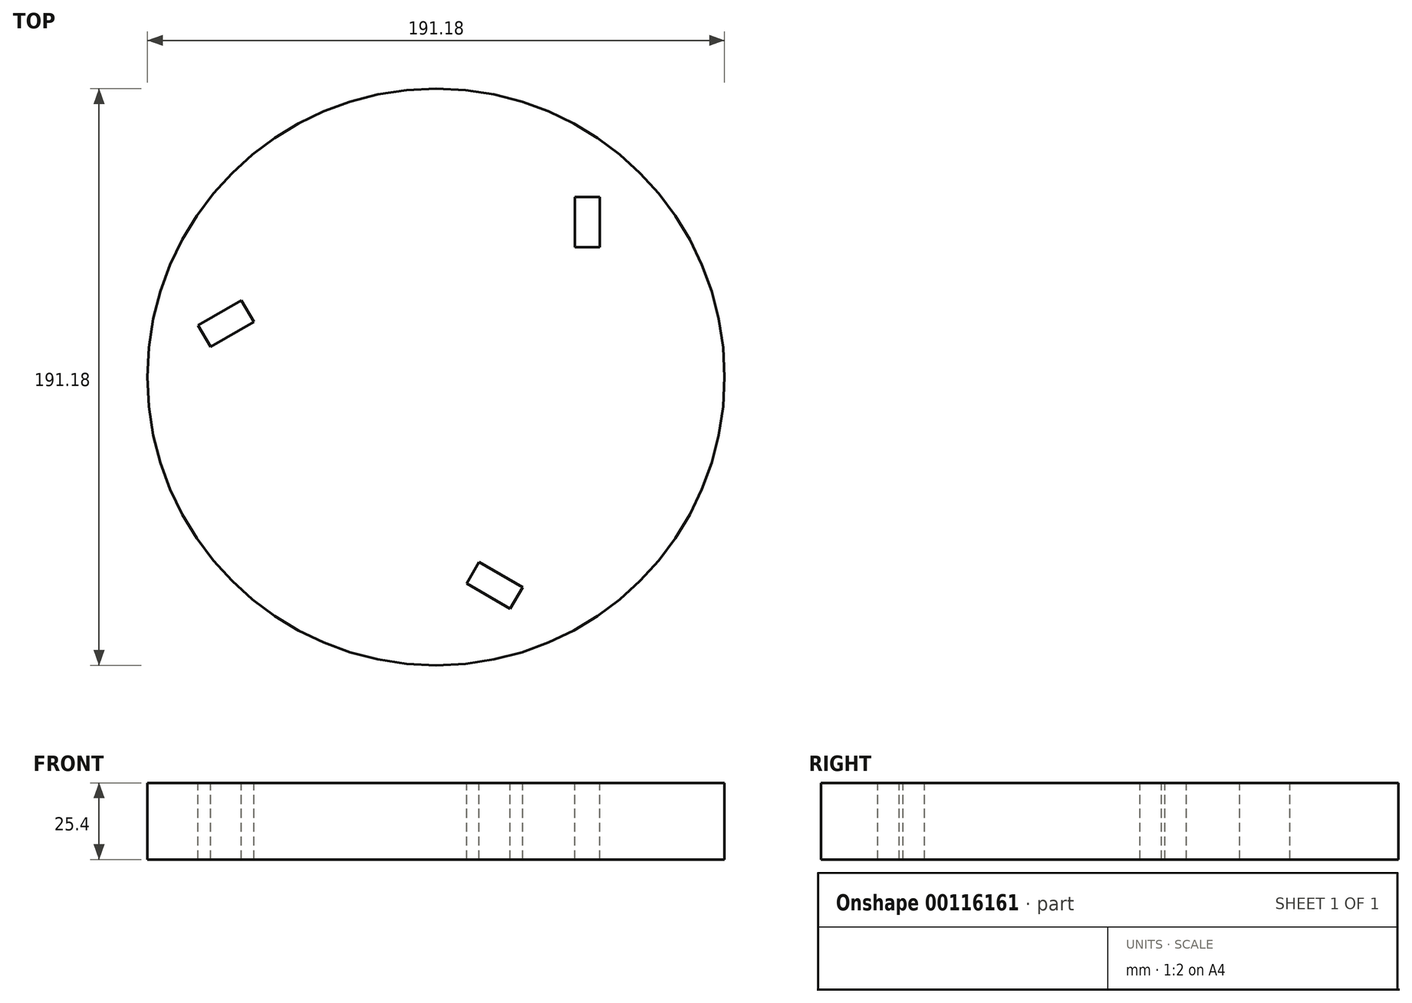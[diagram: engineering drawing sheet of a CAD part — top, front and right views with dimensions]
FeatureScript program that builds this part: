
annotation { "Feature Type Name" : "Feature", "Feature Type Description" : "" }
export const myFeature = defineFeature(function(context is Context, id is Id, definition is map)
    precondition{}
    {
        {
            var Q0;
            Q0=qCreatedBy(makeId("Top.planeOp"),FACE);
            var sketch = newSketch(context, id + "F0", { "sketchPlane" : qUnion([Q0])});
            skLineSegment(sketch, "E0.bottom", {"start": v(54.23, 59.68) * mm, "end": v(46.03, 59.68) * mm});
            skLineSegment(sketch, "E0.top", {"start": v(54.23, 43.09) * mm, "end": v(46.03, 43.09) * mm});
            skLineSegment(sketch, "E0.left", {"start": v(54.23, 59.68) * mm, "end": v(54.23, 43.09) * mm});
            skLineSegment(sketch, "E0.right", {"start": v(46.03, 59.68) * mm, "end": v(46.03, 43.09) * mm});
            skLineSegment(sketch, "E1.1.0", {"start": v(-64.43, 25.43) * mm, "end": v(-60.33, 18.32) * mm});
            skLineSegment(sketch, "E1.1.1", {"start": v(-78.8, 17.13) * mm, "end": v(-64.43, 25.43) * mm});
            skLineSegment(sketch, "E1.1.2", {"start": v(-78.8, 17.13) * mm, "end": v(-74.7, 10.03) * mm});
            skLineSegment(sketch, "E1.1.3", {"start": v(-74.7, 10.03) * mm, "end": v(-60.33, 18.32) * mm});
            skLineSegment(sketch, "E1.2.0", {"start": v(10.2, -68.51) * mm, "end": v(14.3, -61.4) * mm});
            skLineSegment(sketch, "E1.2.1", {"start": v(24.56, -76.8) * mm, "end": v(10.2, -68.51) * mm});
            skLineSegment(sketch, "E1.2.2", {"start": v(24.56, -76.8) * mm, "end": v(28.66, -69.7) * mm});
            skLineSegment(sketch, "E1.2.3", {"start": v(28.66, -69.7) * mm, "end": v(14.3, -61.4) * mm});
            skPoint(sketch, "E1.center", {"position": v(0, 0) * mm});
            skSolve(sketch);
        }
        {
            var Q0;
            Q0=sQuery(id+"F0.wireOp",EDGE,"E1.2.1");
            var Q1;
            Q1 = qBodyType(qCreatedBy(id + "F0" ,EDGE), BodyType.WIRE);
            extrude(context, id + "F3", {"bodyType" : ToolBodyType.SURFACE, "surfaceEntities" : qUnion([Q0, Q1]), "depth" : 25.4 * mm});
        }
        {
            var Q0;
            Q0=qCreatedBy(makeId("Top.planeOp"),FACE);
            var sketch = newSketch(context, id + "F1", { "sketchPlane" : qUnion([Q0])});
            skCircle(sketch, "E2", {"center": v(0, 0) * mm, "radius": 95.59 * mm});
            skSolve(sketch);
        }
        {
            var Q0;
            Q0=makeQuery(id+"F1.imprint","IMPRINT",FACE,{"disambiguationData":[TD([[makeQuery(id+"F1.imprint","IMPRINT",EDGE,{"derivedFrom":sQuery(id+"F1.wireOp",EDGE,"E2")}),1.0]])]});
            var Q1;
            Q1=sQuery(id+"F1.wireOp",EDGE,"E2");
            extrude(context, id + "F2", {"entities" : qUnion([Q0]), "bodyType" : ToolBodyType.SURFACE, "operationType" : NewBodyOperationType.ADD, "surfaceEntities" : qUnion([Q1]), "depth" : 25.4 * mm});
        }
    });
